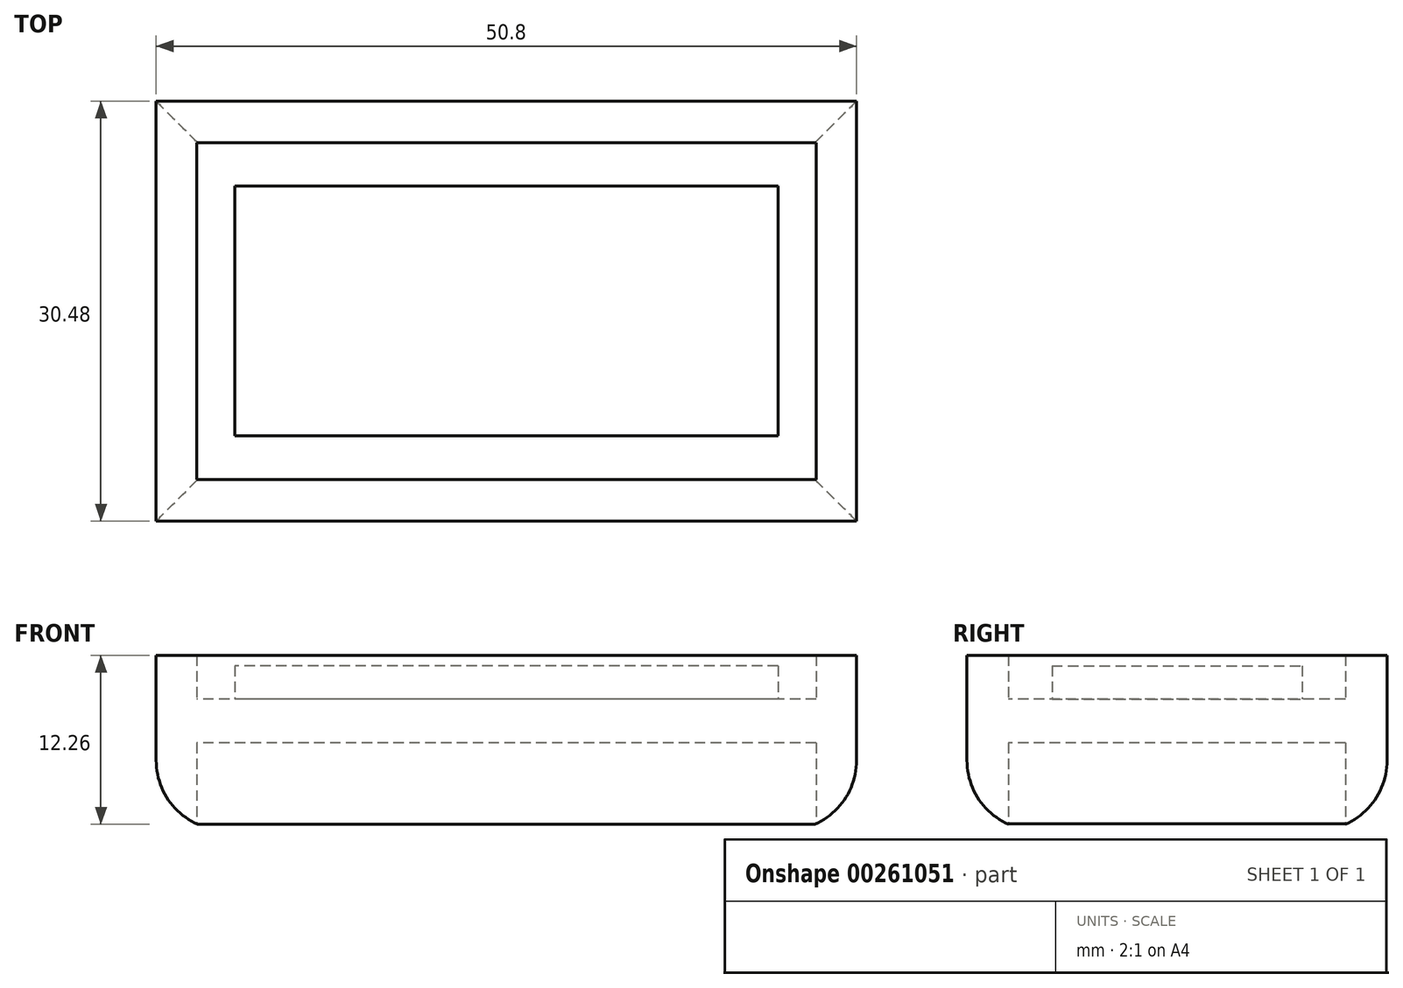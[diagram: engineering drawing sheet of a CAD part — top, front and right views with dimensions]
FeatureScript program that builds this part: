
annotation { "Feature Type Name" : "Feature", "Feature Type Description" : "" }
export const myFeature = defineFeature(function(context is Context, id is Id, definition is map)
    precondition{}
    {
        {
            var Q0;
            Q0=qCreatedBy(makeId("Top.planeOp"),FACE);
            var sketch = newSketch(context, id + "F0", { "sketchPlane" : qUnion([Q0])});
            skLineSegment(sketch, "E0.bottom", {"start": v(25.4, 15.24) * mm, "end": v(-25.4, 15.24) * mm});
            skLineSegment(sketch, "E0.top", {"start": v(25.4, -15.24) * mm, "end": v(-25.4, -15.24) * mm});
            skLineSegment(sketch, "E0.left", {"start": v(25.4, 15.24) * mm, "end": v(25.4, -15.24) * mm});
            skLineSegment(sketch, "E0.right", {"start": v(-25.4, 15.24) * mm, "end": v(-25.4, -15.24) * mm});
            skPoint(sketch, "E0.middle", {"position": v(0, 0) * mm});
            skLineSegment(sketch, "E1.bottom", {"start": v(22.47, 12.22) * mm, "end": v(-22.47, 12.22) * mm});
            skLineSegment(sketch, "E1.top", {"start": v(22.47, -12.22) * mm, "end": v(-22.47, -12.22) * mm});
            skLineSegment(sketch, "E1.left", {"start": v(22.47, 12.22) * mm, "end": v(22.47, -12.22) * mm});
            skLineSegment(sketch, "E1.right", {"start": v(-22.47, 12.22) * mm, "end": v(-22.47, -12.22) * mm});
            skLineSegment(sketch, "E2.bottom", {"start": v(19.7, -9.07) * mm, "end": v(-19.7, -9.07) * mm});
            skLineSegment(sketch, "E2.top", {"start": v(19.7, 9.07) * mm, "end": v(-19.7, 9.07) * mm});
            skLineSegment(sketch, "E2.left", {"start": v(19.7, -9.07) * mm, "end": v(19.7, 9.07) * mm});
            skLineSegment(sketch, "E2.right", {"start": v(-19.7, -9.07) * mm, "end": v(-19.7, 9.07) * mm});
            skSolve(sketch);
        }
        {
            var Q0;
            Q0 = qSketchRegion(id + "F0", true);
            extrude(context, id + "F1", {"entities" : qUnion([Q0]), "endBound" : BoundingType.SYMMETRIC, "depth" : 12.7 * mm});
        }
        {
            var Q0;
            Q0=makeQuery(id+"F0.imprint","IMPRINT",FACE,{"disambiguationData":[TD([[makeQuery(id+"F0.imprint","IMPRINT",EDGE,{"derivedFrom":sQuery(id+"F0.wireOp",EDGE,"E1.bottom")}),1.0]])]});
            extrude(context, id + "F2", {"entities" : qUnion([Q0]), "operationType" : NewBodyOperationType.ADD, "depth" : 3.17 * mm});
        }
        {
            var Q0;
            Q0=makeQuery(id+"F0.imprint","IMPRINT",FACE,{"disambiguationData":[TD([[makeQuery(id+"F0.imprint","IMPRINT",EDGE,{"derivedFrom":sQuery(id+"F0.wireOp",EDGE,"E2.bottom")}),-1.0]])]});
            extrude(context, id + "F3", {"entities" : qUnion([Q0]), "operationType" : NewBodyOperationType.ADD, "depth" : 5.6 * mm});
        }
        {
            var Q0;
            Q0=makeQuery(id+"F1.opExtrude","CAP_EDGE",EDGE,{"disambiguationData":[OSD([sQuery(id+"F0.wireOp",EDGE,"E0.top")])],"isStart":true});
            var Q1;
            Q1=makeQuery(id+"F1.opExtrude","CAP_EDGE",EDGE,{"disambiguationData":[OSD([sQuery(id+"F0.wireOp",EDGE,"E0.bottom")])],"isStart":true});
            var Q2;
            Q2=makeQuery(id+"F1.opExtrude","CAP_EDGE",EDGE,{"disambiguationData":[OSD([sQuery(id+"F0.wireOp",EDGE,"E0.left")])],"isStart":true});
            var Q3;
            Q3=makeQuery(id+"F1.opExtrude","CAP_EDGE",EDGE,{"disambiguationData":[OSD([sQuery(id+"F0.wireOp",EDGE,"E0.right")])],"isStart":true});
            fillet(context, id + "F4", {"entities" : qUnion([Q0, Q1, Q2, Q3]), "radius" : 5.08 * mm, "tangentPropagation" : true, "allowEdgeOverflow" : false});
        }
    });
